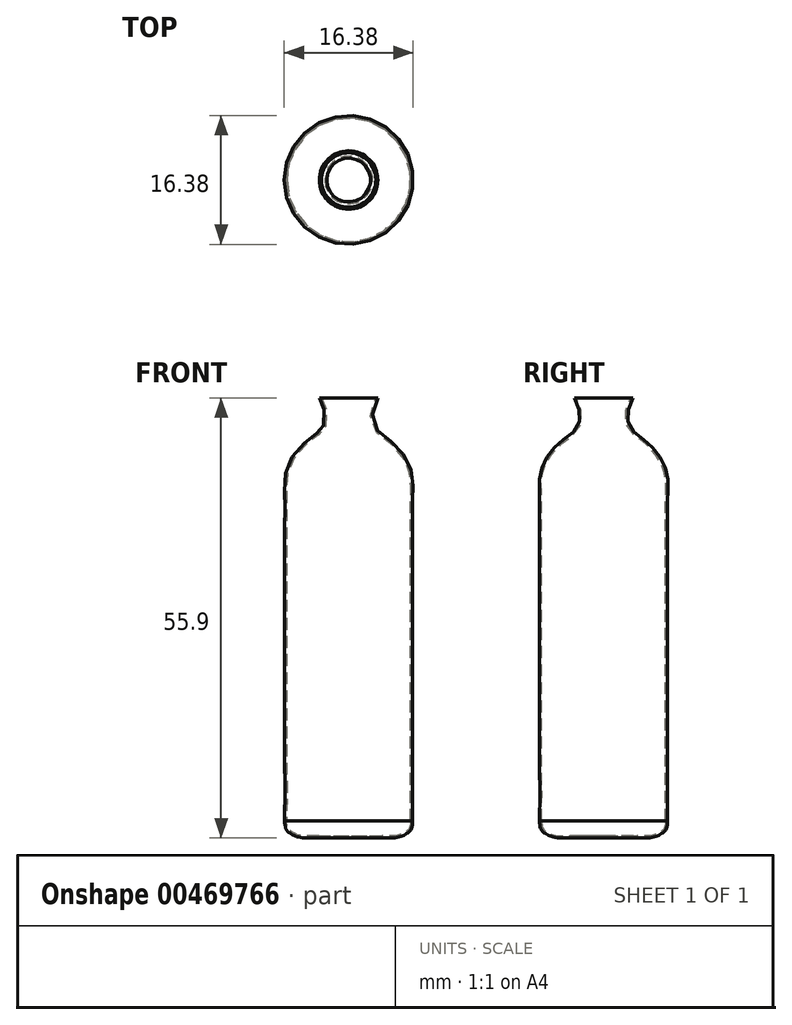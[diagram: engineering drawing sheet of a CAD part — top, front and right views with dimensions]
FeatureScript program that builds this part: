
annotation { "Feature Type Name" : "Feature", "Feature Type Description" : "" }
export const myFeature = defineFeature(function(context is Context, id is Id, definition is map)
    precondition{}
    {
        {
            var Q0;
            Q0=qCreatedBy(makeId("Front.planeOp"),FACE);
            var sketch = newSketch(context, id + "F0", { "sketchPlane" : qUnion([Q0])});
            skLineSegment(sketch, "E0", {"start": v(-5.72, -23.33) * mm, "end": v(-9.5, -23.33) * mm});
            skPoint(sketch, "E1.5.internal.snap0", {"position": v(-7.61, -23.33) * mm});
            skLineSegment(sketch, "E2", {"start": v(-5.72, -23.33) * mm, "end": v(-5.72, 32.57) * mm});
            skLineSegment(sketch, "E3", {"start": v(-5.72, 32.57) * mm, "end": v(-9.43, 32.57) * mm});
            skFitSpline(sketch, "E4", {"points": [v(-9.43, 32.57) * mm, v(-8.92, 31.33) * mm, v(-8.9, 29.05) * mm, v(-9.43, 28.35) * mm, v(-10.76, 27.35) * mm, v(-12.83, 25.15) * mm, v(-13.85, 22.46) * mm, v(-13.85, 19.79) * mm, v(-13.85, 16.89) * mm, v(-13.85, 14.1) * mm, v(-13.85, 11.53) * mm, v(-13.85, 8.63) * mm, v(-13.85, 5.84) * mm, v(-13.85, 3.05) * mm, v(-13.85, 0) * mm, v(-13.85, -4.76) * mm, v(-13.85, -8.22) * mm, v(-13.85, -12.68) * mm, v(-13.85, -21.16) * mm], "startDerivative": vector(-0.68, -33.54) * mm, "endDerivative": vector(-1.5, -96.1) * mm});
            skFitSpline(sketch, "E5", {"points": [v(-9.5, -23.33) * mm, v(-10.55, -23.33) * mm, v(-12.1, -23.23) * mm, v(-12.93, -22.86) * mm, v(-13.6, -22.35) * mm, v(-13.85, -21.16) * mm], "startDerivative": vector(-7.98, -0.19) * mm, "endDerivative": vector(-0.19, 6.38) * mm});
            skSolve(sketch);
        }
        {
            var Q0;
            Q0 = qSketchRegion(id + "F0", true);
            var Q1;
            Q1=sQuery(id+"F0.wireOp",EDGE,"E2");
            revolve(context, id + "F1", {"entities" : qUnion([Q0]), "axis" : qUnion([Q1]), "revolveType" : RevolveType.FULL});
        }
        {
            var Q0;
            Q0=makeQuery(id+"F1.opRevolve","SWEPT_FACE",FACE,{"disambiguationData":[OSD([sQuery(id+"F0.wireOp",EDGE,"E3")])]});
            shell(context, id + "F2", {"entities" : qUnion([Q0]), "thickness" : 0.25 * mm});
        }
    });
